# Revit family: 3400-3401 Trinidad barstool
name_source: partatom
category: Furniture
revit_build: Autodesk Revit 2017 (Build: 20171027_0315(x64)
units: mm (PartAtom-declared; Revit-internal decimal feet)

## family parameters
Always vertical = Yes
Cut with Voids When Loaded = No
OmniClass Number = 23.40.20.00
OmniClass Title = General Furniture and Specialties
Room Calculation Point = No
Shared = No
Work Plane-Based = No

## types (2) — shared parameters
Backrest = FF Ash Black Lacquered vertical
Depth = 50 cm
Description = The precise transparency of the Trinidad chair almost dissolves in a play of light and shadow, yet at the same time gives the chair a strikingly bold voice. The chair without arms is stackable and comes with optional seat upholstery.
Design year = 2017
Designer = Nanna Ditzel
Frame = FF Steel Black
Gliders = FF Plastic Black
Height = 1120,5 cm
Item No. = 3400-3401
Manufacturer = Fredericia Furniture
Model = Trinidad barstool, seat upholstered
Seat = FF Ash Black Lacquered vertical
Seat Height = 77 cm
Seat Upholster = FF Black Leather 88
URL = https://www.fredericia.com
Variation Frame - Extra charge = Available in mat chrome and other frame colours (min. 50 pcs)
Variation Frame - Standard = Available in black, chrome or flint
Variation Height - Extra charge = Frame can be cut of for counter height 102,5 (SH: 68 cm)
Variations Gliders = Available with in felt
Variations Seat - Backrest = Available in black ash, white ash, beech lacquered, oak lacquered, walnut lacquered and light grey / grey / smoked oak stained lacquered
Variations Upholster = Available in Upholster Cushion, in Fabric and Leather
Weight = 5-5,5 kg
Width = 45 cm + 1 cm upholstered seat

## type names
- 3401 Trinidad barstool seat upholstered
- 3400 Trinidad barstool
type visibility flags (boolean, named after types; folded from table):
- 3401 Trinidad barstool seat upholstered: Yes: 3401 Trinidad barstool seat upholstered
- 3400 Trinidad barstool: Yes: 3400 Trinidad barstool seat

## geometry (parser evidence)
native form markers: Sweep x7
no freeform markers — native parametric forms only
